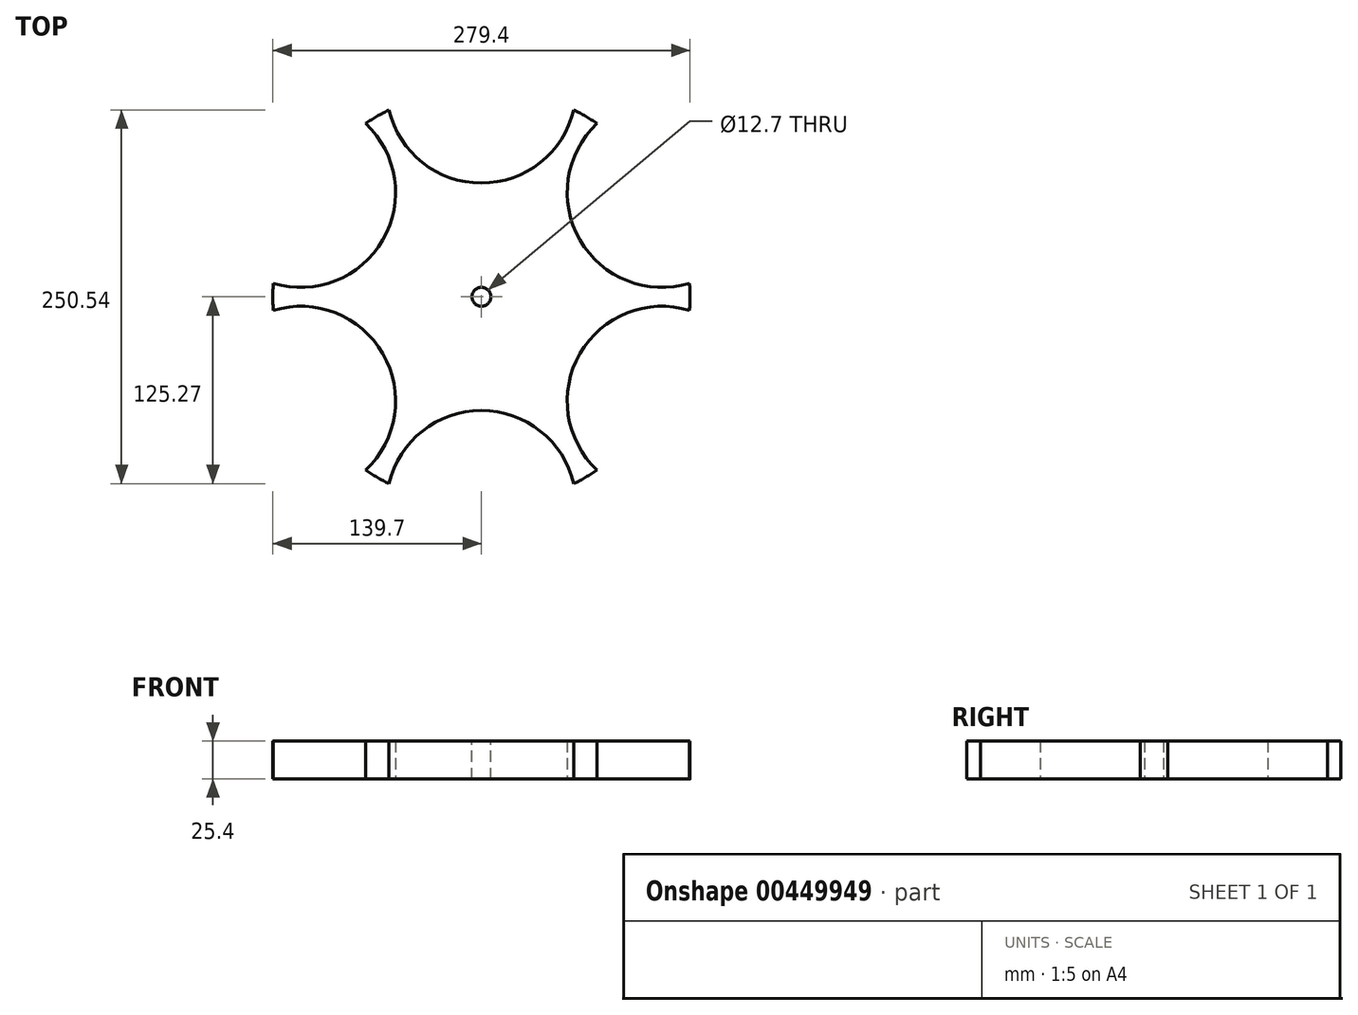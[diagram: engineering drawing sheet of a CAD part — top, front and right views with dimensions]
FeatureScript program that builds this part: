
annotation { "Feature Type Name" : "Feature", "Feature Type Description" : "" }
export const myFeature = defineFeature(function(context is Context, id is Id, definition is map)
    precondition{}
    {
        {
            var Q0;
            Q0=qCreatedBy(makeId("Top.planeOp"),FACE);
            var sketch = newSketch(context, id + "F0", { "sketchPlane" : qUnion([Q0])});
            skCircle(sketch, "E0", {"center": v(0, 0) * mm, "radius": 139.7 * mm});
            skCircle(sketch, "E1", {"center": v(0, 139.7) * mm, "radius": 63.5 * mm});
            skCircle(sketch, "E2", {"center": v(120.98, 69.85) * mm, "radius": 63.5 * mm});
            skCircle(sketch, "E3", {"center": v(120.98, -69.85) * mm, "radius": 63.5 * mm});
            skCircle(sketch, "E4", {"center": v(0, -139.7) * mm, "radius": 63.5 * mm});
            skCircle(sketch, "E5", {"center": v(-120.98, -69.85) * mm, "radius": 63.5 * mm});
            skCircle(sketch, "E6", {"center": v(-120.98, 69.85) * mm, "radius": 63.5 * mm});
            skSolve(sketch);
        }
        {
            var Q0;
            {var subQ0=sQuery(id+"F0.wireOp",EDGE,"E2");var subQ1=sQuery(id+"F0.wireOp",EDGE,"E0");var subQ11=makeQuery(id+"F0.imprint","INTERSECT",VERTEX,{"disambiguationData":[OD(0.0)],"derivedFrom":[subQ1,subQ0]});Q0=makeQuery(id+"F0.imprint","IMPRINT",FACE,{"disambiguationData":[TD([[makeQuery(id+"F0.imprint","IMPRINT",EDGE,{"disambiguationData":[TD([[subQ11,-1.0]])],"derivedFrom":subQ1}),1.0]])]});}
            var sketch = newSketch(context, id + "F1", { "sketchPlane" : qUnion([Q0])});
            skSolve(sketch);
        }
        {
            var Q0;
            Q0 = qSketchRegion(id + "F1", true);
            var Q1;
            {var subQ0=sQuery(id+"F0.wireOp",EDGE,"E2");var subQ1=sQuery(id+"F0.wireOp",EDGE,"E0");var subQ11=makeQuery(id+"F0.imprint","INTERSECT",VERTEX,{"disambiguationData":[OD(0.0)],"derivedFrom":[subQ1,subQ0]});Q1=makeQuery(id+"F0.imprint","IMPRINT",FACE,{"disambiguationData":[TD([[makeQuery(id+"F0.imprint","IMPRINT",EDGE,{"disambiguationData":[TD([[subQ11,-1.0]])],"derivedFrom":subQ1}),1.0]])]});}
            extrude(context, id + "F2", {"entities" : qUnion([Q0, Q1]), "depth" : 25.4 * mm});
        }
        {
            var Q0;
            Q0=makeQuery(id+"F2.opExtrude","CAP_FACE",FACE,{"disambiguationData":[OSD([sQuery(id+"F0.wireOp",EDGE,"E0"),sQuery(id+"F0.wireOp",EDGE,"E1"),sQuery(id+"F0.wireOp",EDGE,"E2"),sQuery(id+"F0.wireOp",EDGE,"E3"),sQuery(id+"F0.wireOp",EDGE,"E4"),sQuery(id+"F0.wireOp",EDGE,"E5"),sQuery(id+"F0.wireOp",EDGE,"E6")])],"isStart":false});
            var sketch = newSketch(context, id + "F3", { "sketchPlane" : qUnion([Q0])});
            skPoint(sketch, "E7", {"position": v(0, 0) * mm});
            skSolve(sketch);
        }
        {
            var Q0;
            Q0=sQuery(id+"F3.wireOp",VERTEX,"E7");
            var Q1;
            Q1=makeQuery(id+"F2.opExtrude","SWEPT_BODY",BODY,{"disambiguationData":[OSD([sQuery(id+"F0.wireOp",EDGE,"E0"),sQuery(id+"F0.wireOp",EDGE,"E1"),sQuery(id+"F0.wireOp",EDGE,"E2"),sQuery(id+"F0.wireOp",EDGE,"E3"),sQuery(id+"F0.wireOp",EDGE,"E4"),sQuery(id+"F0.wireOp",EDGE,"E5"),sQuery(id+"F0.wireOp",EDGE,"E6")])]});
            hole(context, id + "F4", {"style" : HoleStyle.SIMPLE, "endStyle" : HoleEndStyle.BLIND, "holeDiameter" : 12.7 * mm, "holeDepth" : 127 * mm, "isTappedThrough" : true, "tappedDepth" : 12.7 * mm, "tapClearance" : 3, "locations" : qUnion([Q0]), "scope" : qUnion([Q1])});
        }
    });
